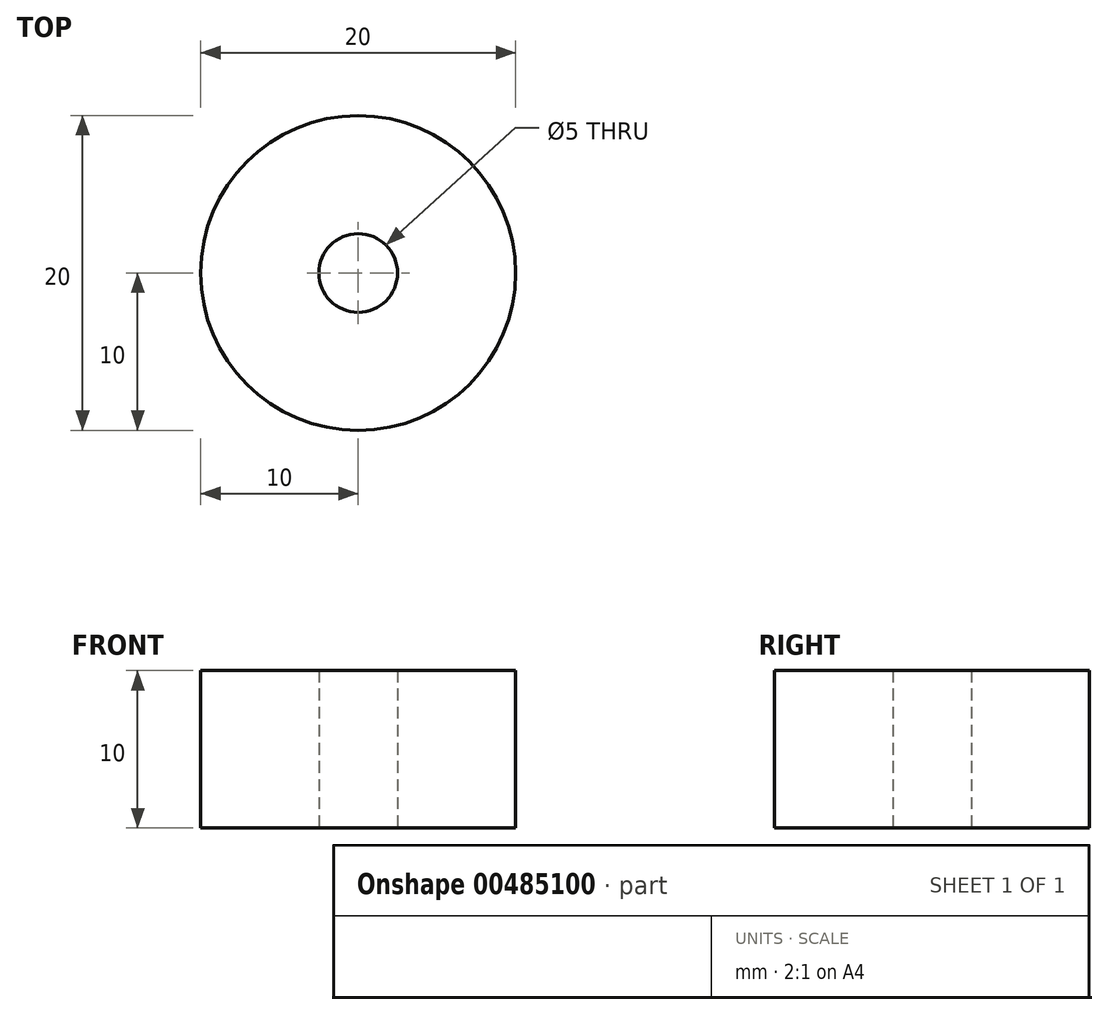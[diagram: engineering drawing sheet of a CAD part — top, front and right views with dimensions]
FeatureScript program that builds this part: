
annotation { "Feature Type Name" : "Feature", "Feature Type Description" : "" }
export const myFeature = defineFeature(function(context is Context, id is Id, definition is map)
    precondition{}
    {
        {
            var Q0;
            Q0=qCreatedBy(makeId("Top.planeOp"),FACE);
            var sketch = newSketch(context, id + "F0", { "sketchPlane" : qUnion([Q0])});
            skCircle(sketch, "E0", {"center": v(0, 0) * mm, "radius": 10 * mm});
            skCircle(sketch, "E1", {"center": v(0, 0) * mm, "radius": 2.5 * mm});
            skSolve(sketch);
        }
        {
            var Q0;
            Q0=makeQuery(id+"F0.imprint","IMPRINT",FACE,{"disambiguationData":[TD([[makeQuery(id+"F0.imprint","IMPRINT",EDGE,{"derivedFrom":sQuery(id+"F0.wireOp",EDGE,"E0")}),1.0]])]});
            extrude(context, id + "F1", {"entities" : qUnion([Q0]), "depth" : 10 * mm, "offsetDistance" : 25 * mm});
        }
    });
